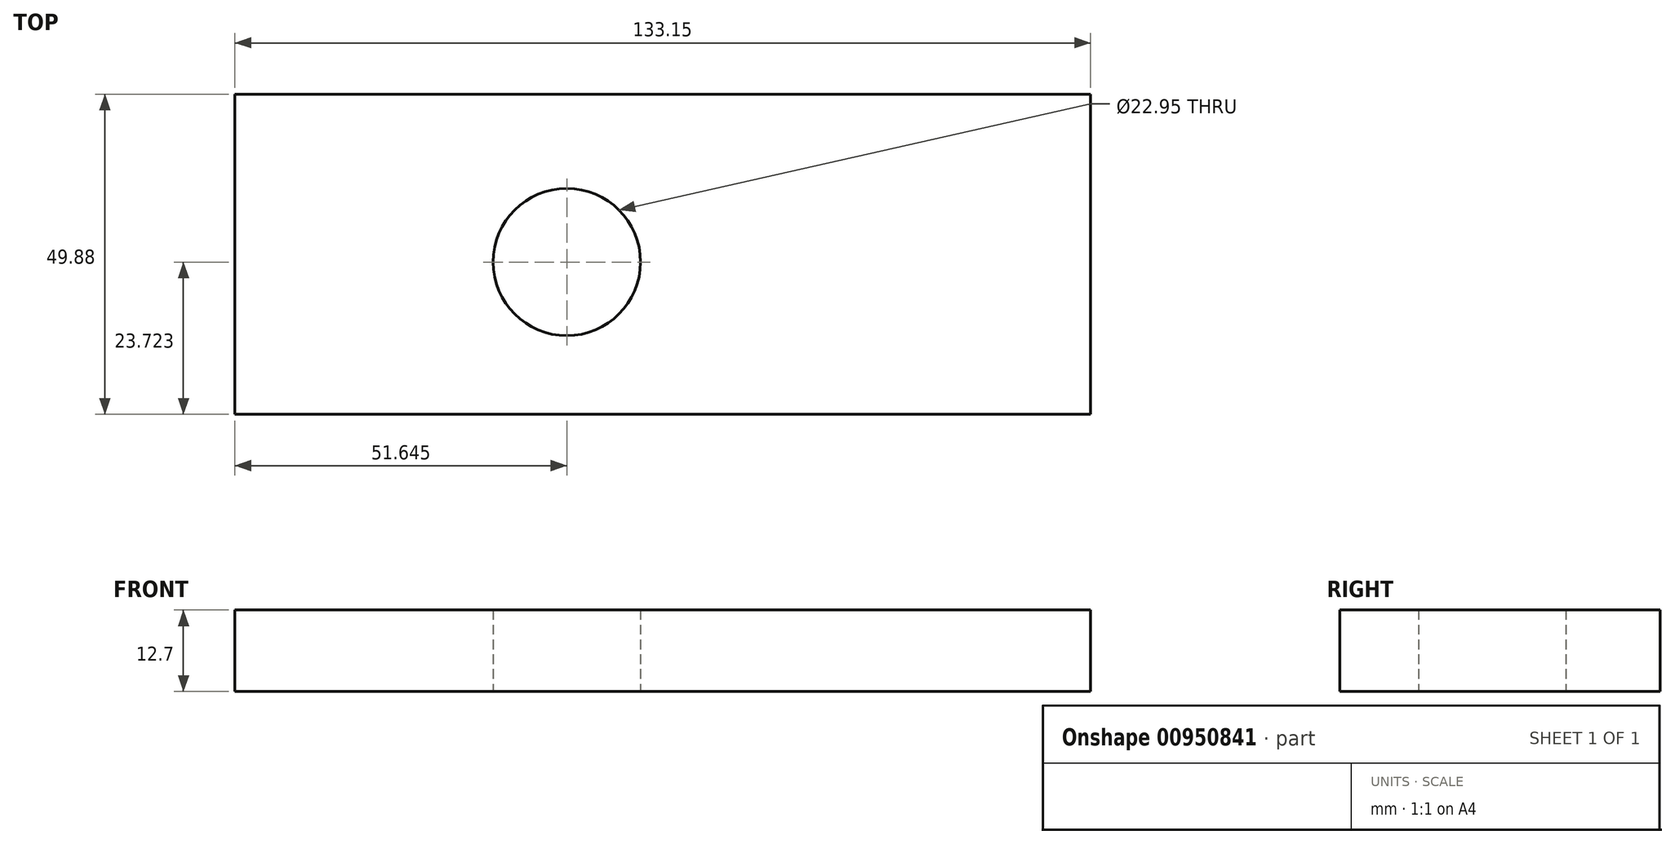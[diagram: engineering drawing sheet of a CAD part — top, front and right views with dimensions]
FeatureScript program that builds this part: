
annotation { "Feature Type Name" : "Feature", "Feature Type Description" : "" }
export const myFeature = defineFeature(function(context is Context, id is Id, definition is map)
    precondition{}
    {
        {
            var Q0;
            Q0=qCreatedBy(makeId("Top.planeOp"),FACE);
            var sketch = newSketch(context, id + "F0", { "sketchPlane" : qUnion([Q0])});
            skLineSegment(sketch, "E0.bottom", {"start": v(0, 0) * mm, "end": v(133.15, 0) * mm});
            skLineSegment(sketch, "E0.top", {"start": v(0, -49.88) * mm, "end": v(133.15, -49.88) * mm});
            skLineSegment(sketch, "E0.left", {"start": v(0, 0) * mm, "end": v(0, -49.88) * mm});
            skLineSegment(sketch, "E0.right", {"start": v(133.15, 0) * mm, "end": v(133.15, -49.88) * mm});
            skCircle(sketch, "E1", {"center": v(51.65, -26.16) * mm, "radius": 11.47 * mm});
            skSolve(sketch);
        }
        {
            var Q0;
            Q0 = qSketchRegion(id + "F0", true);
            extrude(context, id + "F1", {"entities" : qUnion([Q0]), "depth" : 12.7 * mm, "offsetDistance" : 25.4 * mm});
        }
    });
